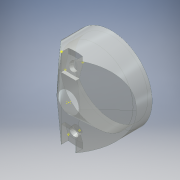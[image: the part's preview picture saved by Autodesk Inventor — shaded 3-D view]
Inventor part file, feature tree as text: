
AUTODESK INVENTOR PART (.ipt)
format: ipt  version: 2016 (Build 200138000, 138)  size: 256,000 bytes
history: native  units: mm
features: other x21, sketch x12, extrude x11, revolve x2, plane x2
ambient origin geometry x8: Origin, YZ Plane, XZ Plane, XY Plane, X Axis, Y Axis, Z Axis, Center Point
bodies: Solid1 (feature_tree)
feature tree (48):
  extrude  "Extrusion1"  Depth=20.0mm TaperAngle=0.0deg
  sketch  "Sketch2"  dims[d3=10.5mm d5=8.5mm]
  extrude  "Extrusion2"  Depth=10.5mm
  extrude  "Extrusion3"  Depth=3.22mm TaperAngle=0.0deg
  revolve  "Revolution1"  [1 undecoded]
  extrude  "Extrusion4"  TaperAngle=90.0deg  [1 undecoded]
  revolve  "Revolution2"  [1 undecoded]
  other  "Work Point1"
  other  "Work Point2"
  plane  "Work Plane1"
  extrude  "Extrusion5"  TaperAngle=90.0deg  [1 undecoded]
  other  "Work Point7"
  plane  "Work Plane4"
  extrude  "Extrusion6"  Depth=4.0mm TaperAngle=0.0deg
  other  "UCS1"
  other  "UCS2"
  sketch  "Sketch20"  dims[d58=0.0mm d59=0.0mm d60=0.0mm d61=0.0mm d62=-1.101303mm d63=0.0mm]
  sketch  "Sketch21"  dims[d67=0.0mm d68=0.0mm d69=0.0mm d70=0.0mm d71=1.101303mm d72=0.0mm d85=12.2mm]
  sketch  "Sketch23"  dims[d90=13.082898mm d91=7.504916mm]
  extrude  "Extrusion13"  Depth=12.2mm
  extrude  "Extrusion14"  Depth=13.082898mm
  extrude  "Extrusion15"  Depth=10.5mm
  extrude  "Extrusion16"  Depth=10.5mm TaperAngle=0.0deg
  extrude  "Extrusion17"  Depth=10.5mm
  sketch  "Sketch1"  dims[d0=38.0mm d1=20.0mm d2=0.0mm]
  sketch  "Sketch3"  dims[d22=8.5mm d24=3.22mm d25=0.0mm]
  sketch  "Sketch4"  dims[d26=3.22mm d27=0.0mm d28=6.1mm]
  sketch  "Sketch5"  dims[d29=1.7mm d30=90.0deg]
  sketch  "Sketch6"  dims[d31=9.62mm d32=3.22mm d33=0.0mm]
  other  "Work Point3"
  sketch  "Sketch10"  dims[d34=7.504916mm d35=90.0deg]
  other  "Work Point8"
  sketch  "Sketch12"  dims[d44=4.0mm d45=0.0mm d47=4.0mm d48=0.0mm]
  sketch  "Sketch25"  dims[d92=7.0mm d93=0.0mm d94=7.504916mm d95=7.0mm d96=0.0mm d97=23.212879mm d98=7.0mm d99=0.0mm d100=23.212879mm d101=7.0mm d102=0.0mm d103=34.0mm d104=6.92mm d105=0.0mm d106=10.5mm d107=3.4mm d110=3.4mm d111=4.0mm d113=3.4mm d114=3.4mm d116=4.0mm d43=1.0mm]
  other  "UCS1: YZ Plane"
  other  "UCS1: XZ Plane"
  other  "UCS1: XY Plane"
  other  "UCS1: X Axis"
  other  "UCS1: Y Axis"
  other  "UCS1: Z Axis"
  other  "UCS1: Center Point"
  other  "UCS2: YZ Plane"
  other  "UCS2: XZ Plane"
  other  "UCS2: XY Plane"
  other  "UCS2: X Axis"
  other  "UCS2: Y Axis"
  other  "UCS2: Z Axis"
  other  "UCS2: Center Point"
note: 4 required parameter values undecoded (feature->parameter linkage not recoverable at this tier; creation-order binding heuristic only, values carry confidence <= 0.55)